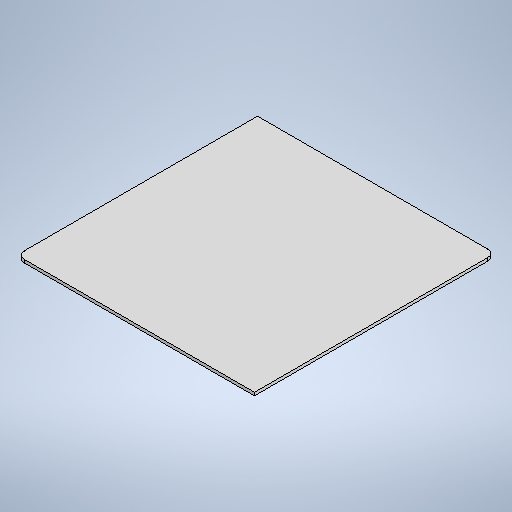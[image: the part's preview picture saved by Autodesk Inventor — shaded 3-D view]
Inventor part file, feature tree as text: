
AUTODESK INVENTOR PART (.ipt)
format: ipt  version: 2025 (Build 290162010, 162A)  size: 224,768 bytes
history: native  units: mm
features: sheet_metal_op x1, chamfer x1, sketch x1, other x1
ambient origin geometry x8: Origin, YZ Plane, XZ Plane, XY Plane, X Axis, Y Axis, Z Axis, Center Point
bodies: Solid1 (feature_tree)
feature tree (4):
  sheet_metal_op  "Face1"
  chamfer  "Corner Round1"
  sketch  "Sketch1"  dims[d0=155.0mm d1=157.0mm d2=2.0mm d3=4.75mm]
  other  "Plate1"
